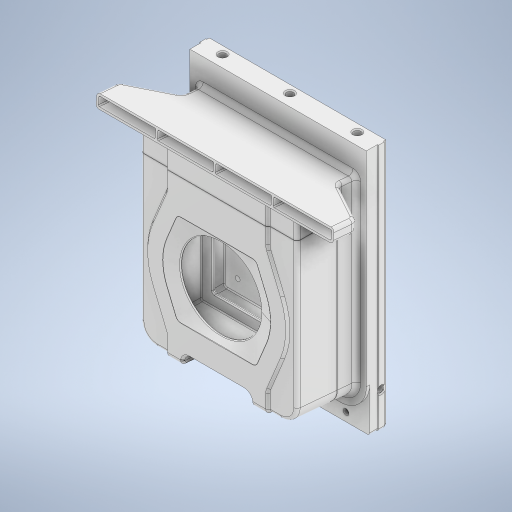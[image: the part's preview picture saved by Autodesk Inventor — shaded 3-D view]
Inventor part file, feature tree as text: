
AUTODESK INVENTOR PART (.ipt)
format: ipt  version: 2024 (Build 280153000, 153)  size: 2,445,824 bytes
history: native  units: mm
features: fillet x42, extrude x36, sketch x35, projected_geometry x30, plane x14, hole x8, other x6, chamfer x5, thicken_offset x5, mirror x2, loft x1, split x1, imported_body x1
ambient origin geometry x8: Origin, YZ Plane, XZ Plane, XY Plane, X Axis, Y Axis, Z Axis, Center Point
bodies: Solid1 (feature_tree)
feature tree (186):
  sketch  "Sketch1"  dims[d0=163.6mm d1=230.0mm]
  extrude  "Extrusion1"  Depth=230.0mm
  extrude  "Extrusion2"  Depth=5.0mm TaperAngle=0.0deg
  extrude  "Extrusion3"  Depth=55.0mm
  extrude  "Extrusion4"  Depth=145.0mm TaperAngle=0.0deg
  fillet  "Fillet1"  [1 undecoded]
  fillet  "Fillet2"  [1 undecoded]
  fillet  "Fillet3"  Radius=20.0mm
  plane  "Work Plane1"
  sketch  "Sketch5"  dims[d8=14.835299mm d9=145.0mm d10=0.0mm d11=120.0deg d12=120.0deg d13=20.0mm]
  plane  "Work Plane2"
  extrude  "Extrusion5"  Depth=220.0mm
  mirror  "Mirror1"
  extrude  "Extrusion6"  Depth=15.0mm
  plane  "Work Plane5"
  sketch  "Sketch9"  dims[d16=12.0mm d17=0.0mm d18=15.0mm]
  extrude  "Extrusion7"  Depth=6.0mm
  extrude  "Extrusion8"  Depth=2.0mm
  plane  "Work Plane6"
  plane  "Work Plane7"
  extrude  "Extrusion9"  [1 undecoded]
  sketch  "Sketch10"  dims[d19=3.0mm d20=6.0mm]
  extrude  "Extrusion10"  Depth=2.0mm
  extrude  "Extrusion11"  Depth=25.5mm
  hole  "Hole1"  [1 undecoded]
  sketch  "Sketch11"  dims[d21=3.0mm d24=2.0mm]
  plane  "Work Plane8"
  extrude  "Extrusion12"  Depth=2.0mm
  hole  "Hole2"  [1 undecoded]
  extrude  "Extrusion13"  Depth=65.0mm TaperAngle=0.0deg
  plane  "Work Plane9"
  loft  "Loft1"
  fillet  "Fillet4"  [1 undecoded]
  fillet  "Fillet5"  Radius=130.0mm
  chamfer  "Chamfer1"  Distance=10.0mm
  sketch  "Sketch15"  dims[d42=2.0mm d43=3.0mm]
  thicken_offset  "Thicken1"
  thicken_offset  "Thicken2"
  thicken_offset  "Thicken3"
  extrude  "Extrusion14"  Depth=10.0mm
  split  "Split1"
  thicken_offset  "Thicken4"
  plane  "Work Plane10"
  extrude  "Extrusion15"  Depth=8.0mm
  extrude  "Extrusion16"  Depth=2.0mm
  extrude  "Extrusion17"  Depth=10.0mm TaperAngle=0.0deg
  extrude  "Extrusion18"  Depth=8.0mm
  fillet  "Fillet6"  Radius=50.0mm
  chamfer  "Chamfer2"  Distance=10.0mm
  extrude  "Extrusion19"  TaperAngle=0.0deg  [1 undecoded]
  fillet  "Fillet7"  [1 undecoded]
  fillet  "Fillet8"  Radius=10.0mm
  extrude  "Extrusion20"  Depth=2.0mm TaperAngle=45.0deg
  extrude  "Extrusion21"  Depth=53.75mm
  extrude  "Extrusion22"  Depth=53.75mm
  sketch  "Sketch27"  dims[d69=105.0mm]
  plane  "Work Plane11"
  extrude  "Extrusion23"  Depth=5.0mm
  extrude  "Extrusion29"  Depth=5.0mm
  fillet  "Fillet9"  Radius=18.0mm
  fillet  "Fillet43"  Radius=27.925268mm
  fillet  "Fillet10"  Radius=24.0mm
  hole  "Hole3"  [1 undecoded]
  hole  "Hole4"  [1 undecoded]
  extrude  "Extrusion24"  Depth=5.0mm TaperAngle=0.0deg
  chamfer  "Chamfer3"  Distance=6.0mm
  mirror  "Mirror2"
  sketch  "Sketch33"  dims[d83=5.3mm d84=6.0mm d85=4.0mm d86=2.0mm d87=90.0deg d88=8.0mm d89=20.594885mm d90=75.0mm d91=50.0mm]
  plane  "Work Plane12"
  plane  "Work Plane14"
  extrude  "Extrusion25"  Depth=5.0mm TaperAngle=0.0deg
  extrude  "Extrusion26"  Depth=5.0mm
  hole  "Hole5"  [1 undecoded]
  sketch  "Sketch34"  dims[d94=135.0deg]
  hole  "Hole6"  [1 undecoded]
  plane  "Work Plane15"
  extrude  "Extrusion27"  Depth=8.0mm
  fillet  "Fillet11"  Radius=8.0mm
  fillet  "Fillet12"  Radius=8.0mm
  fillet  "Fillet13"  Radius=10.0mm
  fillet  "Fillet14"  Radius=65.0mm
  fillet  "Fillet15"  Radius=5.0mm
  fillet  "Fillet16"  Radius=8.0mm
  fillet  "Fillet26"  Radius=180.0mm
  fillet  "Fillet17"  Radius=0.4mm
  fillet  "Fillet19"  Radius=180.0mm
  fillet  "Fillet20"  Radius=101.0mm
  fillet  "Fillet22"  Radius=101.0mm
  fillet  "Fillet23"  [1 undecoded]
  fillet  "Fillet27"  Radius=10.0mm
  extrude  "Extrusion28"  TaperAngle=165.0deg  [1 undecoded]
  fillet  "Fillet28"  Radius=31.0mm
  fillet  "Fillet29"  [1 undecoded]
  fillet  "Fillet30"  Radius=80.0mm
  fillet  "Fillet31"  Radius=80.0mm
  fillet  "Fillet32"  Radius=80.0mm
  fillet  "Fillet33"  Radius=10.0mm
  fillet  "Fillet34"  Radius=125.0mm
  fillet  "Fillet35"  Radius=8.0mm
  fillet  "Fillet36"  Radius=5.5mm
  fillet  "Fillet37"  Radius=1.5mm
  fillet  "Fillet38"  Radius=1.0mm
  fillet  "Fillet39"  Radius=8.5mm
  fillet  "Fillet40"  Radius=6.0mm
  fillet  "Fillet41"  Radius=1.1mm
  fillet  "Fillet42"  Radius=1.0mm
  plane  "Work Plane16"
  extrude  "Extrusion30"  Depth=5.0mm
  sketch  "Sketch41"  dims[d107=1.0mm d108=2.0mm d109=2.0mm d110=45.0deg]
  extrude  "Extrusion31"  Depth=5.0mm
  thicken_offset  "Thicken5"
  fillet  "Fillet44"  [1 undecoded]
  fillet  "Fillet45"  Radius=101.0mm
  fillet  "Fillet46"  Radius=75.0mm
  hole  "Hole7"  [1 undecoded]
  chamfer  "Chamfer4"  Distance=3.0mm
  hole  "Hole8"  [1 undecoded]
  chamfer  "Chamfer5"  Distance=12.0mm
  sketch  "Sketch2"  dims[d2=5.0mm d3=0.0mm d4=13.0mm d5=0.0mm]
  sketch  "Sketch3"  dims[d6=24.5mm d7=55.0mm]
  projected_geometry  "Projected Loop1"
  sketch  "Sketch6"  dims[d14=3.0mm d15=220.0mm]
  sketch  "Sketch12"  dims[d25=10.0mm d26=-2.0mm]
  projected_geometry  "Projected Loop3"
  sketch  "Sketch13"  dims[d27=12.0mm d28=0.0mm d29=2.0mm]
  sketch  "Sketch14"  dims[d32=95.0mm d33=0.0mm d41=25.5mm]
  other  "Srf2"
  other  "Srf3"
  other  "Srf4"
  sketch  "Sketch17"  dims[d44=28.5mm d45=2.0mm]
  projected_geometry  "Projected Loop4"
  projected_geometry  "Projected Loop5"
  projected_geometry  "Projected Loop6"
  sketch  "Sketch18"  dims[d46=125.5mm d48=12.0mm]
  other  "Srf5"
  sketch  "Sketch19"  dims[d49=65.0mm d50=0.0mm d51=65.0mm d52=0.0mm]
  sketch  "Sketch20"  dims[d53=65.0mm d54=-65.0mm d55=10.0mm d56=0.0mm d57=120.0deg d58=130.0mm]
  projected_geometry  "Projected Loop7"
  sketch  "Sketch21"  dims[d59=130.0mm]
  projected_geometry  "Projected Loop8"
  sketch  "Sketch22"  dims[d60=6.0mm]
  sketch  "Sketch23"  dims[d61=120.0deg]
  projected_geometry  "Projected Loop9"
  sketch  "Sketch24"  dims[d62=2.0mm]
  sketch  "Sketch25"  dims[d63=12.0mm d64=10.0mm d65=0.0mm]
  projected_geometry  "Projected Loop10"
  projected_geometry  "Projected Loop11"
  sketch  "Sketch26"  dims[d66=10.0mm d67=0.0mm d68=105.0mm]
  projected_geometry  "Projected Loop12"
  projected_geometry  "Projected Loop13"
  projected_geometry  "Projected Loop14"
  sketch  "Sketch28"  dims[d70=4.4mm d71=6.0mm d72=4.0mm d73=2.0mm d74=90.0deg d75=8.0mm d76=20.594885mm d77=16.0mm]
  sketch  "Sketch30"  dims[d78=6.0mm d79=2.0mm]
  sketch  "Sketch31"  dims[d80=30.0mm d81=10.0mm d82=0.0mm]
  projected_geometry  "Projected Loop15"
  plane  "Work Plane13"
  sketch  "Sketch35"  dims[d95=85.0mm]
  sketch  "Sketch36"  dims[d96=5.0mm]
  sketch  "Sketch38"  dims[d97=16.0mm]
  projected_geometry  "Projected Loop16"
  sketch  "Sketch39"  dims[d98=16.0mm d99=10.0mm d100=0.0mm]
  projected_geometry  "Projected Loop17"
  sketch  "Sketch40"  dims[d101=-4.0mm d102=0.0mm d103=90.0deg d104=0.0mm d105=90.0deg d106=10.0mm]
  other  "Srf6"
  sketch  "Sketch42"  dims[d111=53.75mm d112=53.75mm d113=53.75mm d114=53.75mm d115=12.0mm d116=15.0mm d117=18.0mm d118=27.925268mm d119=24.0mm d120=16.0mm d121=8.0mm d122=6.0mm d123=0.0mm d124=6.0mm d125=0.0mm d126=6.0mm d127=0.0mm d128=2.0mm d129=2.0mm d130=2.0mm d131=8.0mm d132=8.0mm d133=8.0mm d134=10.0mm d135=0.0mm d136=65.0mm d137=5.0mm d138=8.0mm d139=180.0mm d140=0.0mm d141=0.4mm d142=180.0mm d143=101.0mm d144=101.0mm d145=165.0deg d146=10.0mm d147=165.0deg d148=31.0mm d149=0.0mm d150=0.0mm d151=0.0mm d152=80.0mm d153=80.0mm d154=80.0mm d156=10.0mm d157=0.0mm d158=125.0mm d159=8.0mm d160=5.5mm d161=0.0mm d162=1.5mm d163=1.0mm d164=2.0mm d165=45.0deg d166=8.5mm d167=6.0mm d168=0.0mm d169=1.1mm d170=1.0mm d171=0.5mm d172=15.0mm d173=120.0deg d174=101.0mm d175=75.0mm d176=0.0mm d177=75.0mm d178=0.0mm d179=3.0mm d180=0.0mm d181=15.0mm d182=12.0mm d183=-2.0mm d184=10.0mm d185=0.0mm d186=3.0mm d187=2.0mm d188=5.3mm d189=6.0mm d190=4.0mm d191=2.0mm d192=90.0deg d193=8.0mm d194=20.594885mm d195=9.5mm d196=6.0mm d197=4.0mm d198=2.0mm d199=90.0deg d200=8.0mm d201=0.0mm d202=5.5mm d203=6.0mm d204=1.0mm d205=0.0mm d206=1.0mm d207=2.0mm d208=45.0deg d209=53.75mm d210=-1.5mm d211=125.0mm d212=8.25mm d213=-10.0mm d214=7.0mm d215=5.0mm d216=0.0mm d217=10.0mm d218=0.0mm d219=5.4mm d220=6.0mm d221=4.0mm d222=2.0mm d223=90.0deg d224=8.0mm d225=0.0mm d226=184.0mm d227=32.0mm d228=60.0mm d229=60.0mm d230=32.0mm d232=0.2mm d233=8.0mm d234=8.0mm d235=5.4mm d236=6.0mm d237=4.0mm d238=2.0mm d239=90.0deg d240=8.0mm d241=0.0mm d242=-6.0mm d243=8.25mm d244=0.0mm d245=0.0mm d246=4.0mm d247=3.0mm d248=1.0mm d249=2.0mm d250=1.0mm d251=2.0mm d252=3.0mm d254=6.0mm d255=1.0mm d257=1.0mm d258=2.0mm d262=1.0mm d263=5.0mm d264=5.0mm d265=6.0mm d266=0.0mm d267=1.0mm d268=0.5mm d269=1.0mm d270=1.0mm d271=0.5mm d272=1.0mm d273=2.0mm d274=1.0mm d275=10.0mm d276=2.0mm d277=2.0mm d278=1.0mm d279=1.0mm d280=1.0mm d281=1.0mm d282=6.0mm d283=8.0mm d284=8.0mm d285=10.0mm d286=0.0mm d287=3.0mm d288=-19.0mm d289=8.25mm d290=0.0mm d291=0.0mm d292=6.0mm d293=35.0mm d294=20.0mm d295=5.0mm d296=15.0mm d297=135.0deg d298=15.0mm d299=0.0mm d300=0.0mm d301=2.0mm d302=0.0mm d303=4.0mm d304=3.0mm d305=0.0mm d306=1.0mm d307=1.0mm d308=1.0mm d309=5.75mm d310=6.0mm d311=6.5mm d312=11.0mm d313=90.0deg d314=15.0mm d315=20.594885mm d316=1.0mm d317=2.0mm d318=45.0deg d319=5.75mm d320=6.0mm d321=6.5mm d322=11.0mm d323=90.0deg d324=15.0mm d325=20.594885mm d326=1.0mm d327=2.0mm d328=45.0deg d329=7.0mm]
  projected_geometry  "Projected Loop18"
  extrude  "ExtrusionSrf1"  [1 undecoded]
  extrude  "ExtrusionSrf2"  Depth=10.0mm TaperAngle=0.0deg
  extrude  "ExtrusionSrf3"  Depth=5.0mm
  extrude  "ExtrusionSrf4"  Depth=5.0mm
  extrude  "ExtrusionSrf5"  Depth=5.0mm
  projected_geometry  "Project Cut Edges1"
  projected_geometry  "Project Cut Edges3"
  projected_geometry  "Project Cut Edges4"
  projected_geometry  "Project Cut Edges6"
  projected_geometry  "Project Cut Edges7"
  projected_geometry  "Project Cut Edges8"
  projected_geometry  "Project Cut Edges9"
  projected_geometry  "Project Cut Edges10"
  projected_geometry  "Project Cut Edges11"
  other  "CAP"
  imported_body  "BASE"
  projected_geometry  "Project Cut Edges12"
  projected_geometry  "Project Cut Edges13"
  projected_geometry  "Project Cut Edges14"
  projected_geometry  "Project Cut Edges15"
note: 19 required parameter values undecoded (feature->parameter linkage not recoverable at this tier; creation-order binding heuristic only, values carry confidence <= 0.55)
